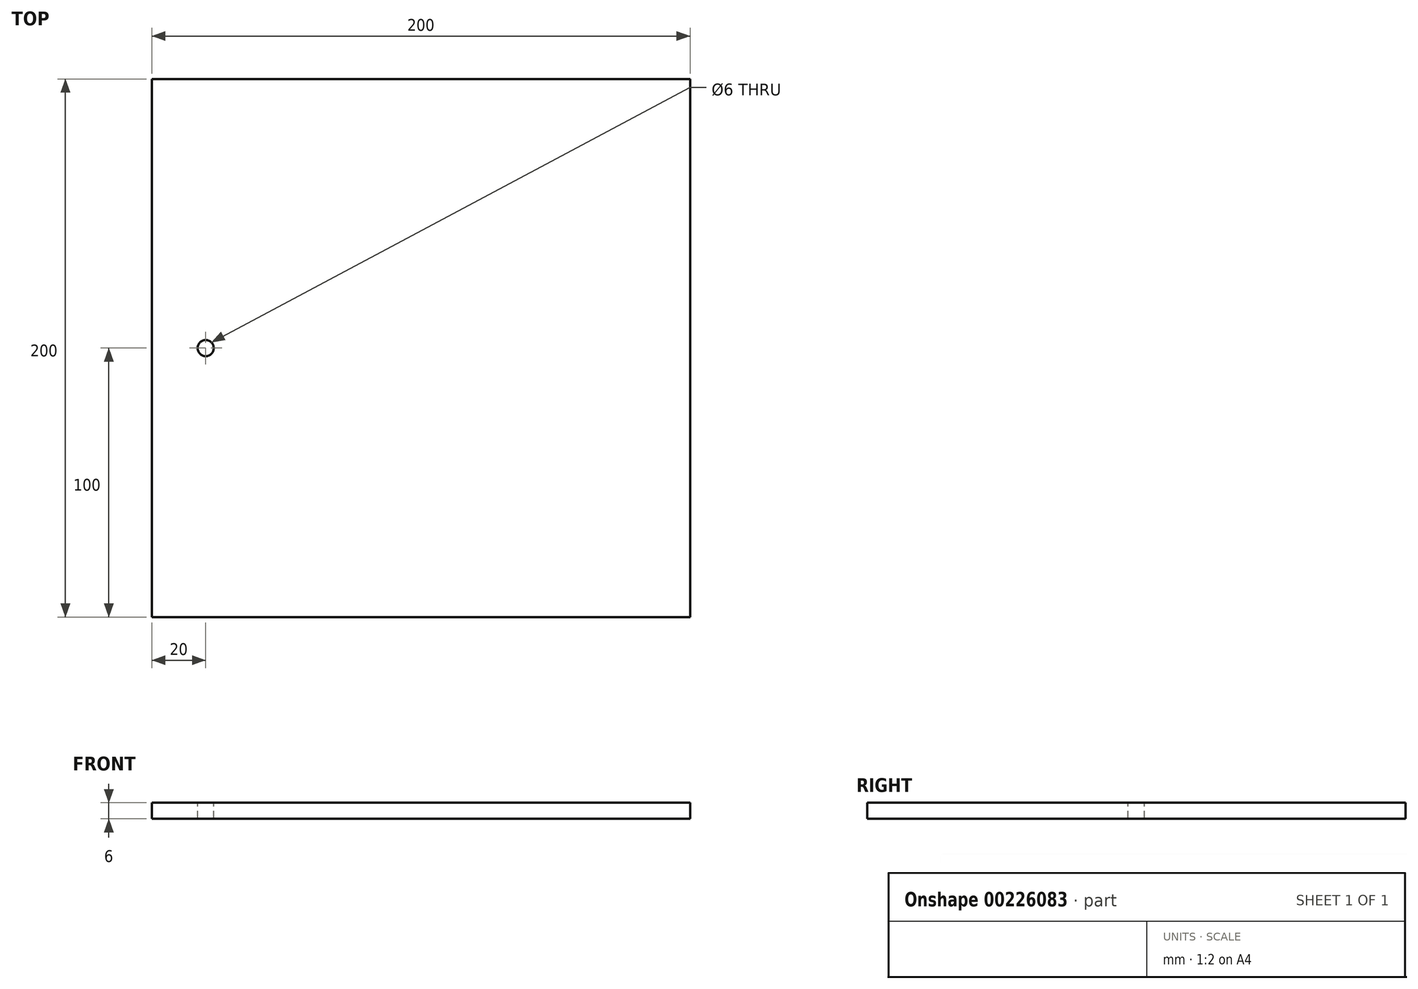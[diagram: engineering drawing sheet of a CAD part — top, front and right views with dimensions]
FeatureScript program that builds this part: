
annotation { "Feature Type Name" : "Feature", "Feature Type Description" : "" }
export const myFeature = defineFeature(function(context is Context, id is Id, definition is map)
    precondition{}
    {
        {
            var Q0;
            Q0=qCreatedBy(makeId("Top.planeOp"),FACE);
            var sketch = newSketch(context, id + "F0", { "sketchPlane" : qUnion([Q0])});
            skLineSegment(sketch, "E0.bottom", {"start": v(0, 0) * mm, "end": v(200, 0) * mm});
            skLineSegment(sketch, "E0.top", {"start": v(0, 200) * mm, "end": v(200, 200) * mm});
            skLineSegment(sketch, "E0.left", {"start": v(0, 0) * mm, "end": v(0, 200) * mm});
            skLineSegment(sketch, "E0.right", {"start": v(200, 0) * mm, "end": v(200, 200) * mm});
            skSolve(sketch);
        }
        {
            var Q0;
            Q0=makeQuery(id+"F0.imprint","IMPRINT",FACE,{"disambiguationData":[TD([[makeQuery(id+"F0.imprint","IMPRINT",EDGE,{"derivedFrom":sQuery(id+"F0.wireOp",EDGE,"E0.bottom")}),1.0]])]});
            extrude(context, id + "F1", {"entities" : qUnion([Q0]), "depth" : 6 * mm});
        }
        {
            var Q0;
            Q0=makeQuery(id+"F1.opExtrude","CAP_FACE",FACE,{"disambiguationData":[OSD([sQuery(id+"F0.wireOp",EDGE,"E0.bottom"),sQuery(id+"F0.wireOp",EDGE,"E0.top"),sQuery(id+"F0.wireOp",EDGE,"E0.left"),sQuery(id+"F0.wireOp",EDGE,"E0.right")])],"isStart":false});
            var sketch = newSketch(context, id + "F2", { "sketchPlane" : qUnion([Q0])});
            skLineSegment(sketch, "E1", {"start": v(0, 200) * mm, "end": v(200, 0) * mm, "construction": true});
            skLineSegment(sketch, "E2", {"start": v(0, 100) * mm, "end": v(200, 100) * mm, "construction": true});
            skCircle(sketch, "E3", {"center": v(20, 100) * mm, "radius": 3 * mm});
            skLineSegment(sketch, "E4", {"start": v(100, 100) * mm, "end": v(100, 141.25) * mm, "construction": true});
            skCircle(sketch, "E5.MirrorC", {"center": v(180, 100) * mm, "radius": 3 * mm});
            skSolve(sketch);
        }
        {
            var Q0;
            Q0=sQuery(id+"F2.wireOp",VERTEX,"E3.center");
            var Q1;
            Q1=sQuery(id+"F2.wireOp",VERTEX,"E5.MirrorC.center");
            var Q2;
            Q2=makeQuery(id+"F1.opExtrude","SWEPT_BODY",BODY,{"disambiguationData":[OSD([sQuery(id+"F0.wireOp",EDGE,"E0.bottom"),sQuery(id+"F0.wireOp",EDGE,"E0.top"),sQuery(id+"F0.wireOp",EDGE,"E0.left"),sQuery(id+"F0.wireOp",EDGE,"E0.right")])]});
            hole(context, id + "F3", {"style" : HoleStyle.SIMPLE, "endStyle" : HoleEndStyle.THROUGH, "holeDiameter" : 6 * mm, "locations" : qUnion([Q0, Q1]), "scope" : qUnion([Q2]), "isTappedThrough" : true});
        }
    });
